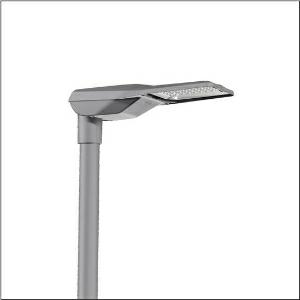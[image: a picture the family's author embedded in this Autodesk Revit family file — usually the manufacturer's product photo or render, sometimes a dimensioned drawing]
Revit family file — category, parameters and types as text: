
# Revit family: streetlight_sl_21_iq_mini___stw1_0a_5xe2e31g08hb_9864
name_source: partatom
category: Lighting Fixtures
units: mm (PartAtom-declared; Revit-internal decimal feet)

## family parameters
Cut with Voids When Loaded = No
Host = Face
Light Source = No
Part Type = Normal
Room Calculation Point = No
Round Connector Dimension = Use Diameter
Shared = No

## types (1)
- --- (1 x LED, 9450 lm, 70.9 W, 3000K)
    Apparent Load = 71 VA
    CIE Flux Codes = 38 75 98 100 100
    Color Rendering = 70
    Color Temperature = 3000K
    Default Elevation = 1800 mm
    Description = Streetlight SL 21 iQ mini, mast luminaire, primary light control with lens, of PMMA, primary optical cover: cover, of toughened safety glass, transparent, light distribution: STW1.0a, light emission: direct distribution, primary light characteristic: asymmetric, installation type: post-top, side-entry, LED, High Power LED, rated luminous flux: 9.450lm, luminous efficacy: 133lm/W, light colour: 730, colour temperature: 3000K, control gear: iQ Street-Remote, control: Street-Remote, Auto-Match, Temp-Guard, Lumen-Switch, Night-Set, Smart-Wire, Light-Fading, Desk-Remote (wireless, voltage-free reading and setting of iQ features in the workshop via application-optimized NFC function/RFID function), optimised constant luminous flux control (CLO 2.0), pre-setting: linear dimming characteristic, mains connection: 220..240V, AC, 50/60Hz, start of lifetime: 71W, end of service life: 75W, reduction: 31W, luminaire housing, of diecast aluminium, powder-coated, SITECO metallic grey (DB 702S), corrosivity category C5 high according to DIN EN ISO 12944, please order mast flange separately, inclination adjustable: 0°, 5°, 10°, 15°, sealing non-destructively replaceable, multi-level sealing system, length: 628mm, width: 235mm, height: 110mm, mast flange for spigot size: 42mm (side-entry): 5XC10008XM4, 60/48mm (side-entry/post-top): 5XC10108XM2, 76/60mm (side-entry/post-top): 5XC10108XM1, mounting height: 4..8m, protection rating (complete): IP66, insulation class (complete): insulation class II (safety insulation), certification: CE, ENEC, ENEC+, VDE, impact resistance: IK10, permissible operating ambient temperature for outdoor applications: -40..+50°C, standard-compliant lighting for roads and squares, packaging unit: 1 piece

Light Distribution: STW1.0a
    Height = 110 mm
    Lamp = 1 x LED
    Lamp Light Flux = 9450 lm
    Lamp Power = 70.9 W
    Lamp count = 1
    Length = 625 mm
    Luminous efficacy = 133 lm/W
    Manufacturer = Siteco
    ModVariant = No
    Model = 5XE2E31G08HB
    Number of Poles = 1
    OnlyDefault = Yes
    Power Factor = 1
    Product Name = Streetlight SL 21 iQ mini | STW1.0a
    Product group = mast luminaire | pylon top
    ProductGroupID = 6100
    Protection Class = Protection class II
    Protection Degree = IP 66
    RLX_Detail_Level = 1
    RLX_Emergency_Light_Flux = 0 lm
    RLX_Emergency_Type = 0
    RLX_Emergency_Type_DB = No
    RlxData = <blob elided: 26445 chars, md5=3eee2314>
    Socket = socket
    Standby Power = 0 W
    System Light Flux = 9450 lm
    System Power = 71 W
    Type Comments = factory setting: luminous flux: 100 % | dim-lin: 254 | 711 mA
    Type Image = l_1003519.jpg
    URL = http://relux.com
    VarID = @adj_157299
    Voltage = 0 V
    Weight = 0.00 kg
    Width = 234 mm

## geometry (parser evidence)
native form markers: Blend x4, Sweep x13
no freeform markers — native parametric forms only
